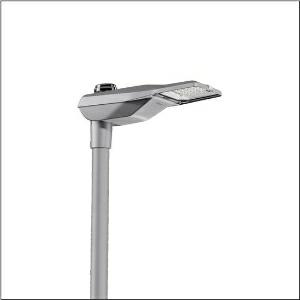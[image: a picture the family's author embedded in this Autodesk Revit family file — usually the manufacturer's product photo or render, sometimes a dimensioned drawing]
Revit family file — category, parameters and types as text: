
# Revit family: streetlight_sl_21_micro___stw1_0a_5xe5e47n08cb_41ee
name_source: partatom
category: Lighting Fixtures
units: mm (PartAtom-declared; Revit-internal decimal feet)

## family parameters
Cut with Voids When Loaded = No
Host = Face
Light Source = No
Part Type = Normal
Room Calculation Point = No
Round Connector Dimension = Use Diameter
Shared = No

## types (1)
- --- (1 x LED, 2380 lm, 15.8 W, 4000K)
    Apparent Load = 16 VA
    CIE Flux Codes = 38 75 98 100 100
    Color Rendering = 70
    Color Temperature = 4000K
    Default Elevation = 1800 mm
    Description = Streetlight SL 21 micro, mast luminaire, primary light control with lens, of PMMA, primary optical cover: cover, of toughened safety glass, transparent, light distribution: STW1.0a, light emission: direct distribution, primary light characteristic: asymmetric, installation type: post-top, LED, 3G 1.5mm², High Power LED, rated luminous flux: 2.380lm, luminous efficacy: 151lm/W, light colour: 740, colour temperature: 4000K, control gear: NEMA (7pin), control: overheat protection, pre-setting: linear dimming characteristic, constant luminous flux control, time-dependent luminous flux control, flexible luminous flux parameterisation, mains connection: 230..240V, AC, 50/60Hz, connection cable pre-assembled, cable length: 6,5m, wiring characteristics: H07RN-F, start of lifetime: 16W, end of service life: 16W, reduction: 8W, luminaire housing, of diecast aluminium (EN AC-44300), powder-coated, SITECO metallic grey (DB 702S), corrosivity category C5 high according to DIN EN ISO 12944, multi-level sealing system, sealing non-destructively replaceable, inclination adjustable: 0°, 5°, 10°, 15°, length: 528mm, width: 235mm, height: 110mm, spigot size: 76/60mm (post-top), mounting height: 4..8m, protection rating (complete): IP66, insulation class (complete): insulation class I (protective earthing), certification: CE, ENEC, ENEC+, VDE, impact resistance: IK10, permissible operating ambient temperature for outdoor applications: -40..+50°C, standard-compliant lighting for roads and squares, packaging unit: 1 piece

Light Distribution: STW1.0a
    Height = 110 mm
    Lamp = 1 x LED
    Lamp Light Flux = 2380 lm
    Lamp Power = 15.8 W
    Lamp count = 1
    Length = 528 mm
    Luminous efficacy = 151 lm/W
    Manufacturer = Siteco
    ModVariant = No
    Model = 5XE5E47N08CB
    Number of Poles = 1
    OnlyDefault = Yes
    Power Factor = 1
    Product Name = Streetlight SL 21 micro | STW1.0a
    Product group = mast luminaire | pylon top
    ProductGroupID = 6100
    Protection Class = Protection class I
    Protection Degree = IP 66
    RLX_Detail_Level = 1
    RLX_Emergency_Light_Flux = 0 lm
    RLX_Emergency_Type = 0
    RLX_Emergency_Type_DB = No
    RlxData = <blob elided: 98201 chars, md5=b3e64fa9>
    Socket = socket
    Standby Power = 0 W
    System Light Flux = 2380 lm
    System Power = 16 W
    Type Comments = factory setting: luminous flux: 100 % | dim-lin: 254 | 300 mA
    Type Image = l_1294375.jpg
    URL = http://relux.com
    VarID = @adj_135287
    Voltage = 0 V
    Weight = 0.00 kg
    Width = 235 mm

## geometry (parser evidence)
native form markers: Blend x4, Sweep x11
no freeform markers — native parametric forms only
